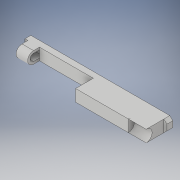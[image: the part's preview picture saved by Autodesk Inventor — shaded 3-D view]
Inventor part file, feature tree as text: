
AUTODESK INVENTOR PART (.ipt)
format: ipt  version: 2018 (Build 220112000, 112)  size: 142,336 bytes
history: native  units: in
note: dims shown in document units (in); Inventor stores cm internally (conversion verified against a paired STEP export)
features: extrude x4, sketch x4, chamfer x1, fillet x1, shell x1
ambient origin geometry x8: Origin, YZ Plane, XZ Plane, XY Plane, X Axis, Y Axis, Z Axis, Center Point
bodies: Solid1 (feature_tree)
feature tree (11):
  extrude  "Extrusion1"  Depth=0.5in
  chamfer  "Chamfer1"  Distance=0.25in
  extrude  "Extrusion2"  Depth=0.5in TaperAngle=0.0deg
  fillet  "Fillet1"  Radius=0.25in
  shell  "Shell1"  Thickness=0.1in
  extrude  "Extrusion3"  Depth=0.75in TaperAngle=0.0deg
  extrude  "Extrusion4"  [1 undecoded]
  sketch  "Sketch1"  dims[d0=6.0in d1=0.5in d2=0.25in d3=0.0in]
  sketch  "Sketch2"  dims[d4=0.125in d5=0.125in d6=45.0deg d13=0.5in d14=0.0in d15=0.25in d16=0.1in]
  sketch  "Sketch3"  dims[d17=0.75in d18=0.0in d19=0.75in d20=0.0in]
  sketch  "Sketch4"
note: 1 required parameter value undecoded (feature->parameter linkage not recoverable at this tier; creation-order binding heuristic only, values carry confidence <= 0.55)
